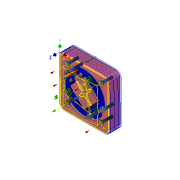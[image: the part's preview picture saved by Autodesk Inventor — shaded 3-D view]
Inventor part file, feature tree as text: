
AUTODESK INVENTOR PART (.ipt)
format: ipt  version: 2022 (Build 260153000, 153)  size: 1,213,440 bytes
history: native  units: mm
features: projected_geometry x17, sketch x7, other x5, hole x3, extrude x3, reference x2
ambient origin geometry x8: Origin, YZ Plane, XZ Plane, XY Plane, X Axis, Y Axis, Z Axis, Center Point
bodies: Volumenkörper1 (feature_tree)
feature tree (37):
  other  "IM_Mold_plate.ipt"
  sketch  "Skizze1"  dims[d0=10.0mm]
  hole  "Bohrung1"  [1 undecoded]
  extrude  "Extrusion1"  Depth=8.0mm
  hole  "Bohrung2"  [1 undecoded]
  hole  "Bohrung3"  [1 undecoded]
  extrude  "Extrusion2"  [1 undecoded]
  extrude  "Extrusion3"  [1 undecoded]
  other  "Volumenkörper5::IM_Mold_plate.ipt"
  other  "Bezeichnung1"
  reference  "Referenz1"
  sketch  "Skizze2"  dims[d1=6.0mm d2=6.0mm d3=8.0mm d4=1.0mm d5=90.0deg d6=8.0mm d7=20.594885mm d8=1.0mm d9=0.0mm]
  reference  "Referenz2"
  projected_geometry  "Projizierte Kontur1"
  sketch  "Skizze3"  dims[d10=3.2mm d11=6.0mm d12=6.5mm d13=3.0mm d14=90.0deg d15=8.0mm d16=20.594885mm]
  projected_geometry  "Projizierte Kontur2"
  sketch  "Skizze4"  dims[d17=3.7mm d18=6.0mm d19=6.5mm d20=3.0mm d21=90.0deg d22=8.0mm d23=20.594885mm d24=8.0mm d25=0.174533mm]
  projected_geometry  "Projizierte Kontur3"
  sketch  "Skizze5"  dims[d26=16.015316mm d27=10.0mm d28=0.0mm]
  projected_geometry  "Projizierte Kontur4"
  sketch  "Skizze6"
  projected_geometry  "Projizierte Kontur5"
  projected_geometry  "Projizierte Kontur6"
  projected_geometry  "Projizierte Kontur7"
  projected_geometry  "Projizierte Kontur8"
  projected_geometry  "Projizierte Kontur9"
  projected_geometry  "Projizierte Kontur10"
  projected_geometry  "Projizierte Kontur11"
  projected_geometry  "Projizierte Kontur12"
  projected_geometry  "Projizierte Kontur13"
  projected_geometry  "Projizierte Kontur14"
  sketch  "Skizze7"
  projected_geometry  "Projizierte Kontur15"
  projected_geometry  "Projizierte Kontur16"
  projected_geometry  "Projizierte Kontur17"
  other  "IM_Mold_plate_top.ipt.iam"
  other  "IM_Mold_plate:1"
note: 5 required parameter values undecoded (feature->parameter linkage not recoverable at this tier; creation-order binding heuristic only, values carry confidence <= 0.55)
